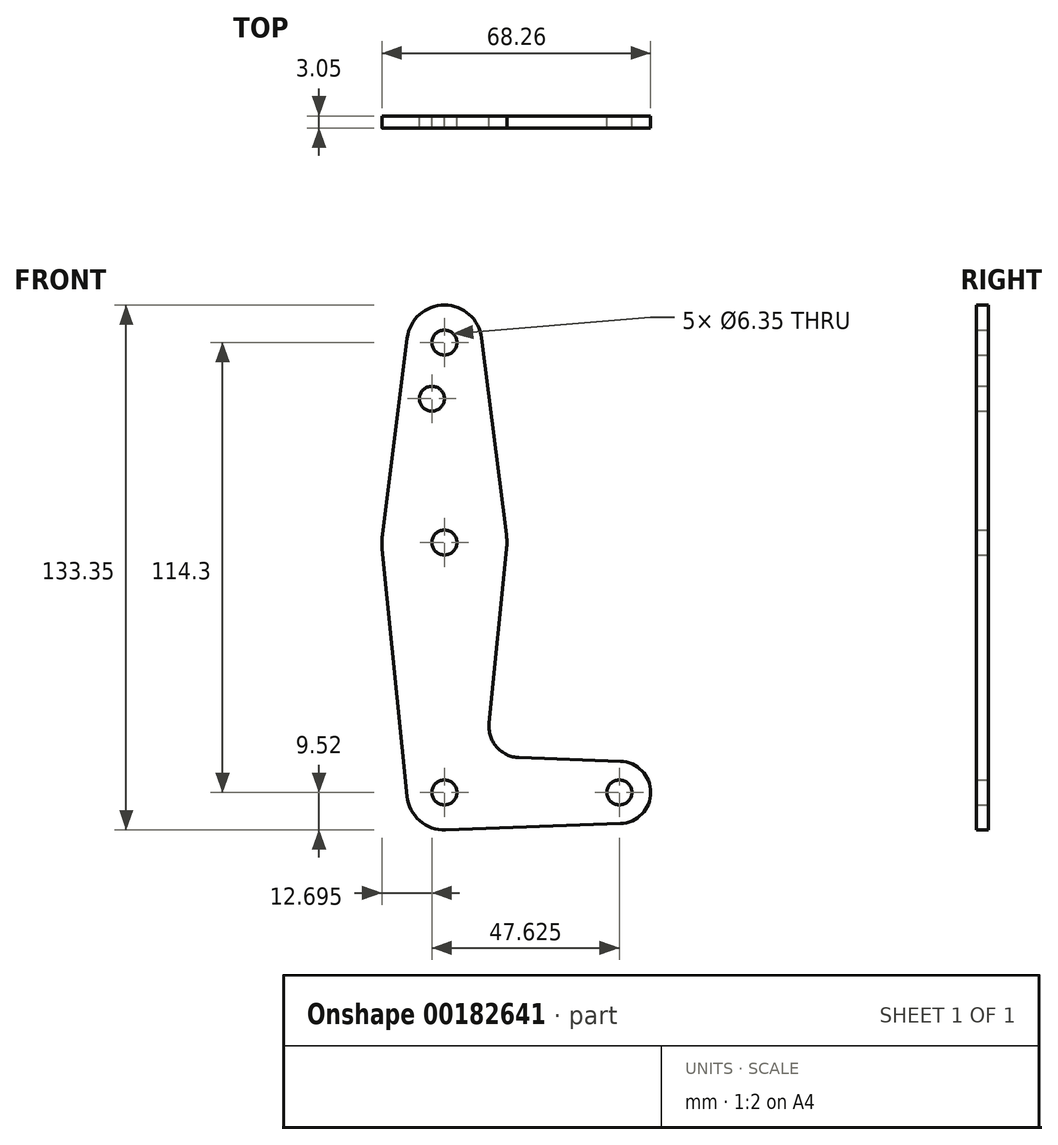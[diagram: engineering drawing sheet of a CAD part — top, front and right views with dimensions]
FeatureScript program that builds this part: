
annotation { "Feature Type Name" : "Feature", "Feature Type Description" : "" }
export const myFeature = defineFeature(function(context is Context, id is Id, definition is map)
    precondition{}
    {
        {
            var Q0;
            Q0=qCreatedBy(makeId("Front.planeOp"),FACE);
            var sketch = newSketch(context, id + "F0", { "sketchPlane" : qUnion([Q0])});
            skLineSegment(sketch, "E0", {"start": v(0, 0) * mm, "end": v(0, 114.3) * mm, "construction": true});
            skLineSegment(sketch, "E1", {"start": v(0, 0) * mm, "end": v(44.45, 0) * mm, "construction": true});
            skCircle(sketch, "E2", {"center": v(0, 114.3) * mm, "radius": 9.53 * mm});
            skCircle(sketch, "E3", {"center": v(0, 63.5) * mm, "radius": 15.88 * mm});
            skCircle(sketch, "E4", {"center": v(0, 0) * mm, "radius": 9.53 * mm});
            skCircle(sketch, "E5", {"center": v(44.45, 0) * mm, "radius": 7.94 * mm});
            skLineSegment(sketch, "E6", {"start": v(-9.45, 115.5) * mm, "end": v(-15.75, 65.48) * mm});
            skLineSegment(sketch, "E7", {"start": v(9.45, 115.5) * mm, "end": v(15.75, 65.48) * mm});
            skLineSegment(sketch, "E8", {"start": v(-15.8, 61.91) * mm, "end": v(-9.48, -0.95) * mm});
            skLineSegment(sketch, "E9", {"start": v(15.8, 61.91) * mm, "end": v(11.34, 17.6) * mm});
            skLineSegment(sketch, "E10", {"start": v(18.97, 8.85) * mm, "end": v(44.73, 7.93) * mm});
            skLineSegment(sketch, "E11", {"start": v(0.34, -9.52) * mm, "end": v(44.73, -7.93) * mm});
            skCircle(sketch, "E12", {"center": v(0, 114.3) * mm, "radius": 3.18 * mm});
            skCircle(sketch, "E13", {"center": v(0, 63.5) * mm, "radius": 3.18 * mm});
            skCircle(sketch, "E14", {"center": v(0, 0) * mm, "radius": 3.18 * mm});
            skCircle(sketch, "E15", {"center": v(44.45, 0) * mm, "radius": 3.18 * mm});
            skArc(sketch, "E16.filletArc", {"start": v(11.34, 17.6) * mm, "mid": v(13.26, 11.57) * mm, "end": v(18.97, 8.85) * mm});
            skCircle(sketch, "E17", {"center": v(-3.18, 100.03) * mm, "radius": 3.18 * mm});
            skSolve(sketch);
        }
        {
            var Q0;
            {var subQ1=sQuery(id+"F0.wireOp",EDGE,"E6");Q0=makeQuery(id+"F0.imprint","IMPRINT",FACE,{"disambiguationData":[TD([[makeQuery(id+"F0.imprint","IMPRINT",EDGE,{"derivedFrom":subQ1}),1.0]])]});}
            var Q1;
            Q1=makeQuery(id+"F0.imprint","IMPRINT",FACE,{"disambiguationData":[TD([[makeQuery(id+"F0.imprint","IMPRINT",EDGE,{"derivedFrom":sQuery(id+"F0.wireOp",EDGE,"E12")}),-1.0]])]});
            var Q2;
            Q2=makeQuery(id+"F0.imprint","IMPRINT",FACE,{"disambiguationData":[TD([[makeQuery(id+"F0.imprint","IMPRINT",EDGE,{"derivedFrom":sQuery(id+"F0.wireOp",EDGE,"E13")}),-1.0]])]});
            var Q3;
            {var subQ0=sQuery(id+"F0.wireOp",EDGE,"E8");Q3=makeQuery(id+"F0.imprint","IMPRINT",FACE,{"disambiguationData":[TD([[makeQuery(id+"F0.imprint","IMPRINT",EDGE,{"derivedFrom":subQ0}),1.0]])]});}
            var Q4;
            Q4=makeQuery(id+"F0.imprint","IMPRINT",FACE,{"disambiguationData":[TD([[makeQuery(id+"F0.imprint","IMPRINT",EDGE,{"derivedFrom":sQuery(id+"F0.wireOp",EDGE,"E14")}),-1.0]])]});
            var Q5;
            Q5=makeQuery(id+"F0.imprint","IMPRINT",FACE,{"disambiguationData":[TD([[makeQuery(id+"F0.imprint","IMPRINT",EDGE,{"derivedFrom":sQuery(id+"F0.wireOp",EDGE,"E15")}),-1.0]])]});
            extrude(context, id + "F1", {"entities" : qUnion([Q0, Q1, Q2, Q3, Q4, Q5]), "depth" : 3.05 * mm});
        }
    });
